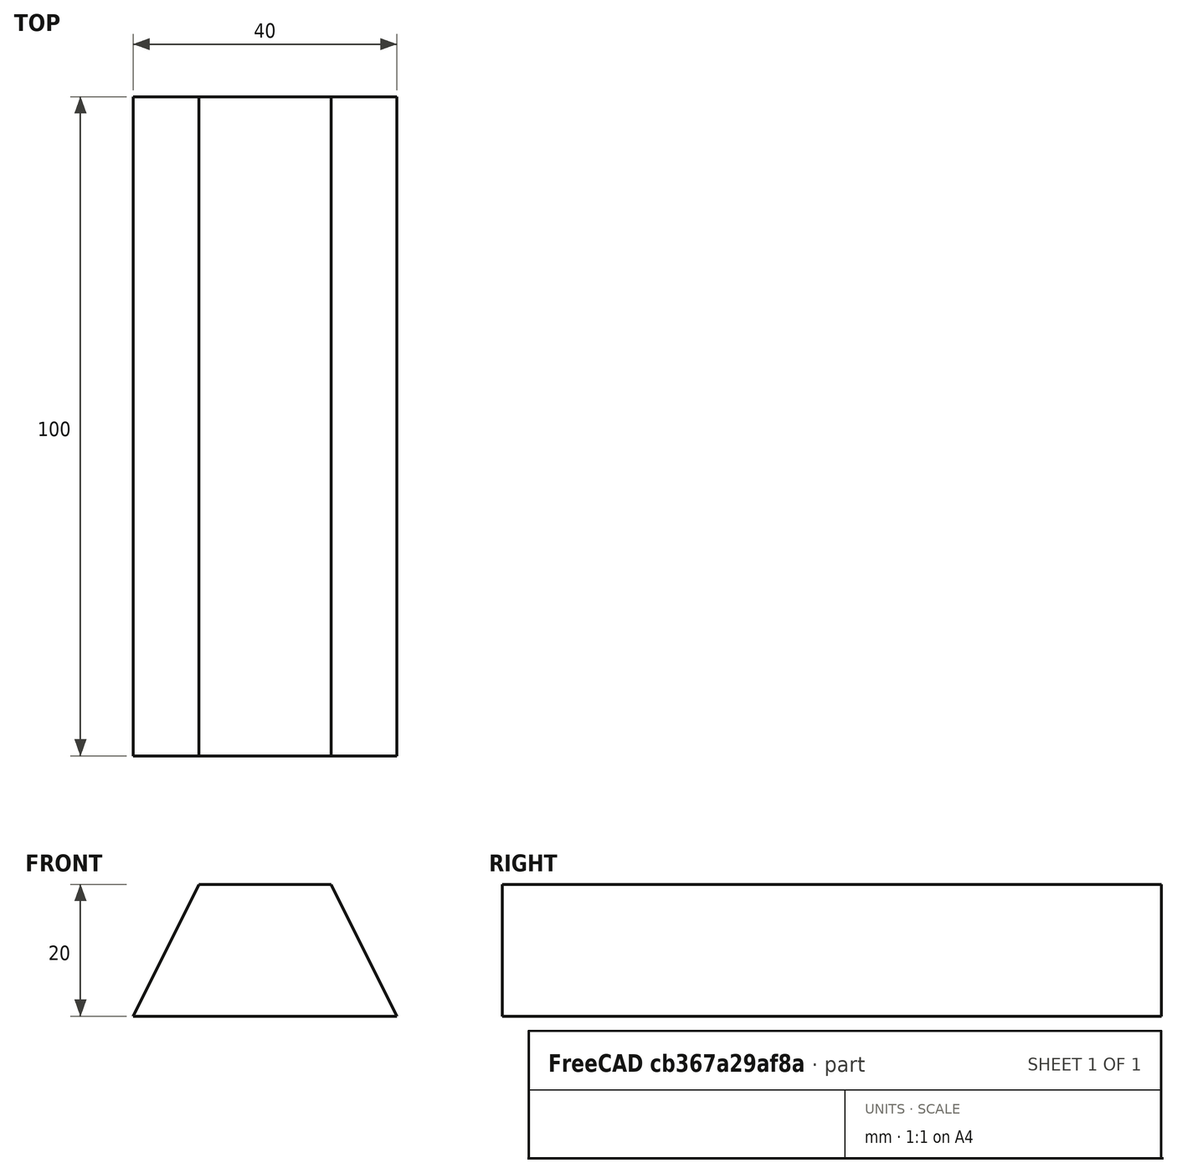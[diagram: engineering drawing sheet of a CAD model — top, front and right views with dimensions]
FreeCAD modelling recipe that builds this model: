
FCSTD DOCUMENT  (FreeCAD 0.16R6707 (Git))
Label: Lingote
License: CreativeCommons Attribution-ShareAlike
LicenseURL: http://creativecommons.org/licenses/by-sa/4.0/
objects: Sketcher::SketchObject×1, PartDesign::Pad×1
note: 3 computed .brp shape members not serialized (recipe doc carries the construction recipe); baked Part::Feature solids carry a one-line shape summary decoded from their .brp

FEATURE [Sketcher::SketchObject] Sketch  label="Boceto_Lingote"
  Placement = pos=(0,0,0) rot=(1,0,0;1.5708rad)
  sketch-geometry (4):
    g0: LineSegment StartX=-20 StartY=0 StartZ=0 EndX=-10 EndY=20 EndZ=0
    g1: LineSegment StartX=-10 StartY=20 StartZ=0 EndX=10 EndY=20 EndZ=0
    g2: LineSegment StartX=10 StartY=20 StartZ=0 EndX=20 EndY=0 EndZ=0
    g3: LineSegment StartX=20 StartY=0 StartZ=0 EndX=-20 EndY=0 EndZ=0
  constraints (4):
    c: Coincident(g0,g1)
    c: Coincident(g1,g2)
    c: Coincident(g2,g3)
    c: Coincident(g3,g0)
FEATURE [PartDesign::Pad] Pad  label="Lingote"
  Length = 100
  Length2 = 100
  Placement = pos=(0,0,0) rot=(1,0,0;1.5708rad)
  Sketch = -> Sketch
  Type = 0
